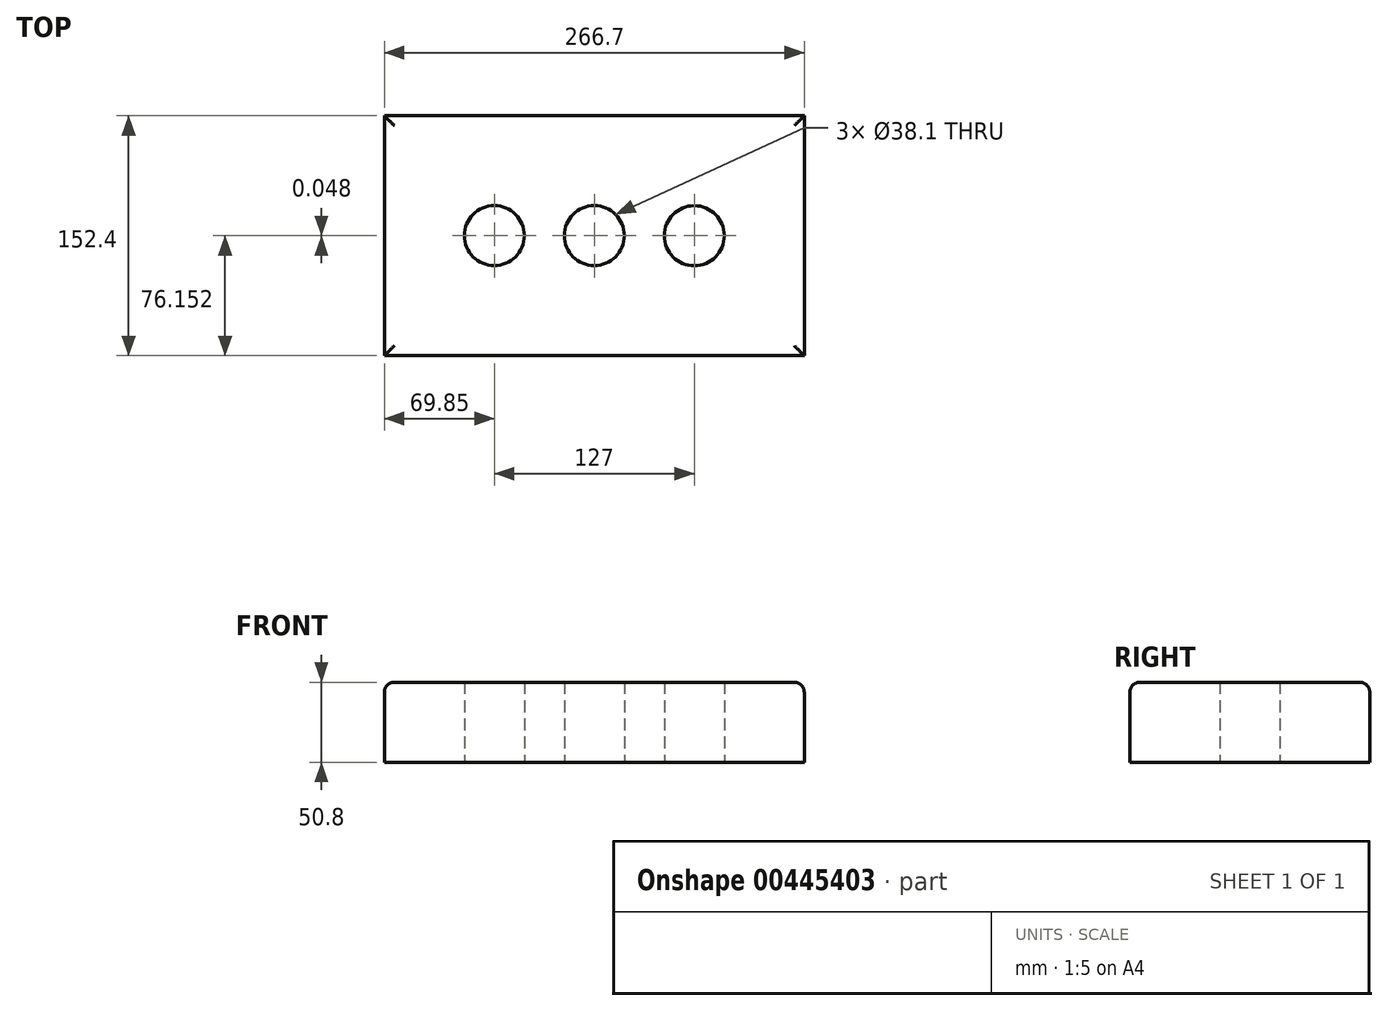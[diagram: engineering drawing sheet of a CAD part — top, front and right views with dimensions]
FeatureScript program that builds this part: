
annotation { "Feature Type Name" : "Feature", "Feature Type Description" : "" }
export const myFeature = defineFeature(function(context is Context, id is Id, definition is map)
    precondition{}
    {
        {
            var Q0;
            Q0=qCreatedBy(makeId("Top.planeOp"),FACE);
            var sketch = newSketch(context, id + "F0", { "sketchPlane" : qUnion([Q0])});
            skLineSegment(sketch, "E0.bottom", {"start": v(133.35, -76.2) * mm, "end": v(-133.35, -76.2) * mm});
            skLineSegment(sketch, "E0.top", {"start": v(133.35, 76.2) * mm, "end": v(-133.35, 76.2) * mm});
            skLineSegment(sketch, "E0.left", {"start": v(133.35, -76.2) * mm, "end": v(133.35, 76.2) * mm});
            skLineSegment(sketch, "E0.right", {"start": v(-133.35, -76.2) * mm, "end": v(-133.35, 76.2) * mm});
            skPoint(sketch, "E0.middle", {"position": v(0, 0) * mm});
            skCircle(sketch, "E1", {"center": v(0, 0) * mm, "radius": 19.05 * mm});
            skLineSegment(sketch, "E2", {"start": v(19.05, 0) * mm, "end": v(44.45, 0) * mm});
            skLineSegment(sketch, "E3", {"start": v(-19.05, 0) * mm, "end": v(-44.45, 0) * mm});
            skCircle(sketch, "E4", {"center": v(-63.5, 0) * mm, "radius": 19.05 * mm});
            skPoint(sketch, "E4.second.point", {"position": v(-82.55, 0.13) * mm});
            skPoint(sketch, "E4.third.point", {"position": v(-75.85, 14.5) * mm});
            skCircle(sketch, "E5", {"center": v(63.5, -0.05) * mm, "radius": 19.05 * mm});
            skPoint(sketch, "E5.second.point", {"position": v(61.93, 18.94) * mm});
            skPoint(sketch, "E5.third.point", {"position": v(78.74, -11.48) * mm});
            skLineSegment(sketch, "E6", {"start": v(0, 0) * mm, "end": v(-63.5, 0) * mm});
            skSolve(sketch);
        }
        {
            var Q0;
            Q0=makeQuery(id+"F0.imprint","IMPRINT",FACE,{"disambiguationData":[TD([[makeQuery(id+"F0.imprint","IMPRINT",EDGE,{"derivedFrom":sQuery(id+"F0.wireOp",EDGE,"E0.bottom")}),-1.0]])]});
            extrude(context, id + "F1", {"entities" : qUnion([Q0]), "depth" : 50.8 * mm});
        }
        {
            var Q0;
            Q0=makeQuery(id+"F1.opExtrude","CAP_EDGE",EDGE,{"disambiguationData":[OSD([sQuery(id+"F0.wireOp",EDGE,"E0.bottom")])],"isStart":false});
            var Q1;
            Q1=makeQuery(id+"F1.opExtrude","CAP_EDGE",EDGE,{"disambiguationData":[OSD([sQuery(id+"F0.wireOp",EDGE,"E0.left")])],"isStart":false});
            var Q2;
            Q2=makeQuery(id+"F1.opExtrude","CAP_EDGE",EDGE,{"disambiguationData":[OSD([sQuery(id+"F0.wireOp",EDGE,"E0.top")])],"isStart":false});
            var Q3;
            Q3=makeQuery(id+"F1.opExtrude","CAP_EDGE",EDGE,{"disambiguationData":[OSD([sQuery(id+"F0.wireOp",EDGE,"E0.right")])],"isStart":false});
            fillet(context, id + "F2", {"entities" : qUnion([Q0, Q1, Q2, Q3]), "radius" : 6.35 * mm, "tangentPropagation" : true, "allowEdgeOverflow" : false});
        }
    });
